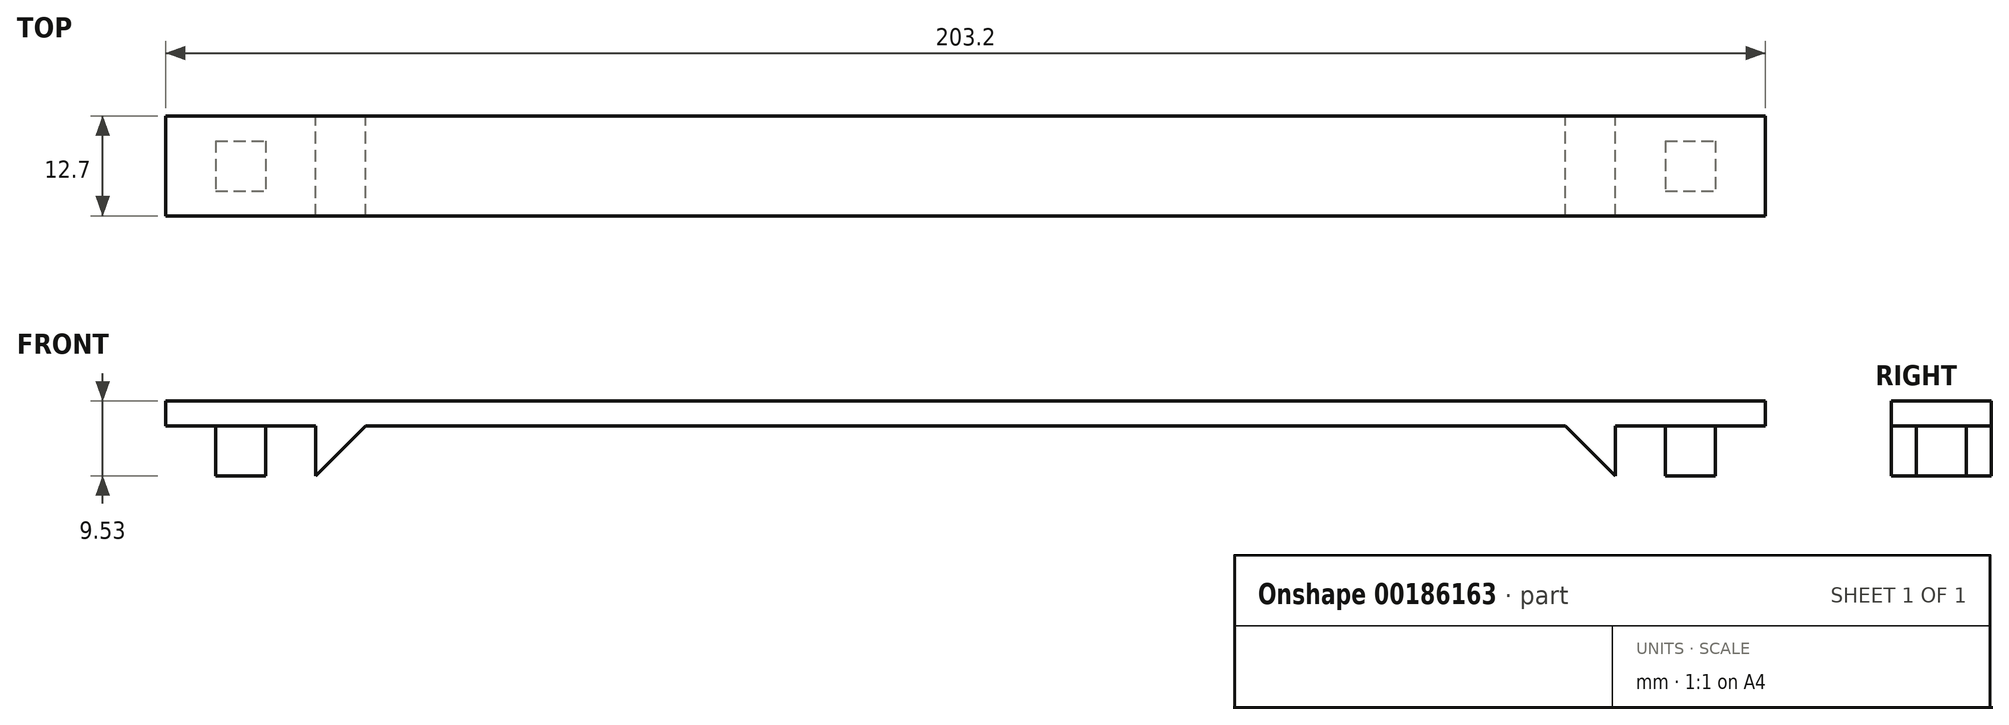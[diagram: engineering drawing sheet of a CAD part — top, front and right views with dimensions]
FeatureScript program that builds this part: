
annotation { "Feature Type Name" : "Feature", "Feature Type Description" : "" }
export const myFeature = defineFeature(function(context is Context, id is Id, definition is map)
    precondition{}
    {
        {
            var Q0;
            Q0=qCreatedBy(makeId("Top.planeOp"),FACE);
            var sketch = newSketch(context, id + "F0", { "sketchPlane" : qUnion([Q0])});
            skLineSegment(sketch, "E0.bottom", {"start": v(101.6, 6.35) * mm, "end": v(-101.6, 6.35) * mm});
            skLineSegment(sketch, "E0.top", {"start": v(101.6, -6.35) * mm, "end": v(-101.6, -6.35) * mm});
            skLineSegment(sketch, "E0.left", {"start": v(101.6, 6.35) * mm, "end": v(101.6, -6.35) * mm});
            skLineSegment(sketch, "E0.right", {"start": v(-101.6, 6.35) * mm, "end": v(-101.6, -6.35) * mm});
            skPoint(sketch, "E0.middle", {"position": v(0, 0) * mm});
            skSolve(sketch);
        }
        {
            var Q0;
            Q0 = qSketchRegion(id + "F0", true);
            extrude(context, id + "F1", {"entities" : qUnion([Q0]), "depth" : 9.52 * mm});
        }
        {
            var Q0;
            Q0=makeQuery(id+"F1.opExtrude","SWEPT_FACE",FACE,{"disambiguationData":[OSD([sQuery(id+"F0.wireOp",EDGE,"E0.bottom")])]});
            var sketch = newSketch(context, id + "F2", { "sketchPlane" : qUnion([Q0])});
            skLineSegment(sketch, "E1.bottom", {"start": v(-101.6, 0) * mm, "end": v(-82.55, 0) * mm});
            skLineSegment(sketch, "E1.top", {"start": v(-101.6, 6.35) * mm, "end": v(-82.55, 6.35) * mm});
            skLineSegment(sketch, "E1.left", {"start": v(-101.6, 0) * mm, "end": v(-101.6, 6.35) * mm});
            skLineSegment(sketch, "E1.right", {"start": v(-82.55, 0) * mm, "end": v(-82.55, 6.35) * mm});
            skLineSegment(sketch, "E2", {"start": v(101.6, 0) * mm, "end": v(82.55, 0) * mm});
            skLineSegment(sketch, "E3.top", {"start": v(101.6, 6.35) * mm, "end": v(82.55, 6.35) * mm});
            skLineSegment(sketch, "E3.left", {"start": v(101.6, 0) * mm, "end": v(101.6, 6.35) * mm});
            skLineSegment(sketch, "E3.right", {"start": v(82.55, 0) * mm, "end": v(82.55, 6.35) * mm});
            skSolve(sketch);
        }
        {
            var Q0;
            Q0 = qSketchRegion(id + "F2", true);
            extrude(context, id + "F3", {"entities" : qUnion([Q0]), "operationType" : NewBodyOperationType.REMOVE, "oppositeDirection" : true, "depth" : 25.4 * mm});
        }
        {
            var Q0;
            Q0=makeQuery(id+"F1.opExtrude","CAP_FACE",FACE,{"disambiguationData":[OSD([sQuery(id+"F0.wireOp",EDGE,"E0.bottom"),sQuery(id+"F0.wireOp",EDGE,"E0.top"),sQuery(id+"F0.wireOp",EDGE,"E0.left"),sQuery(id+"F0.wireOp",EDGE,"E0.right")])],"isStart":true});
            var sketch = newSketch(context, id + "F4", { "sketchPlane" : qUnion([Q0])});
            skLineSegment(sketch, "E4.bottom", {"start": v(-88.9, 3.17) * mm, "end": v(-95.25, 3.17) * mm});
            skLineSegment(sketch, "E4.top", {"start": v(-88.9, -3.17) * mm, "end": v(-95.25, -3.17) * mm});
            skLineSegment(sketch, "E4.left", {"start": v(-88.9, 3.17) * mm, "end": v(-88.9, -3.17) * mm});
            skLineSegment(sketch, "E4.right", {"start": v(-95.25, 3.17) * mm, "end": v(-95.25, -3.17) * mm});
            skPoint(sketch, "E4.middle", {"position": v(-92.08, 0) * mm});
            skLineSegment(sketch, "E5.bottom", {"start": v(95.25, 3.18) * mm, "end": v(88.9, 3.18) * mm});
            skLineSegment(sketch, "E5.top", {"start": v(95.25, -3.17) * mm, "end": v(88.9, -3.17) * mm});
            skLineSegment(sketch, "E5.left", {"start": v(95.25, 3.18) * mm, "end": v(95.25, -3.17) * mm});
            skLineSegment(sketch, "E5.right", {"start": v(88.9, 3.18) * mm, "end": v(88.9, -3.17) * mm});
            skPoint(sketch, "E5.middle", {"position": v(92.08, 0) * mm});
            skSolve(sketch);
        }
        {
            var Q0;
            Q0 = qSketchRegion(id + "F4", true);
            var Q1;
            Q1=makeQuery(id+"F3.boolean.opBoolean","COPY",FACE,{"derivedFrom":makeQuery(id+"F3.opExtrude","SWEPT_FACE",FACE,{"disambiguationData":[OSD([sQuery(id+"F2.wireOp",EDGE,"E1.top")])]})});
            extrude(context, id + "F5", {"entities" : qUnion([Q0]), "operationType" : NewBodyOperationType.ADD, "endBound" : BoundingType.UP_TO_SURFACE, "oppositeDirection" : true, "endBoundEntityFace" : qUnion([Q1]), "depth" : 25.4 * mm});
        }
        {
            var Q0;
            Q0=makeQuery(id+"F1.opExtrude","SWEPT_FACE",FACE,{"disambiguationData":[OSD([sQuery(id+"F0.wireOp",EDGE,"E0.bottom")])]});
            var sketch = newSketch(context, id + "F6", { "sketchPlane" : qUnion([Q0])});
            skLineSegment(sketch, "E6", {"start": v(82.55, 0) * mm, "end": v(76.2, 6.35) * mm});
            skLineSegment(sketch, "E7", {"start": v(76.2, 6.35) * mm, "end": v(-76.2, 6.35) * mm});
            skLineSegment(sketch, "E8", {"start": v(-76.2, 6.35) * mm, "end": v(-82.55, 0) * mm});
            skLineSegment(sketch, "E9", {"start": v(82.55, 0) * mm, "end": v(-82.55, 0) * mm});
            skSolve(sketch);
        }
        {
            var Q0;
            Q0=makeQuery(id+"F6.imprint","IMPRINT",FACE,{"disambiguationData":[TD([[makeQuery(id+"F6.imprint","IMPRINT",EDGE,{"derivedFrom":sQuery(id+"F6.wireOp",EDGE,"E6")}),1.0]])]});
            extrude(context, id + "F7", {"entities" : qUnion([Q0]), "operationType" : NewBodyOperationType.REMOVE, "oppositeDirection" : true, "depth" : 25.4 * mm});
        }
    });
